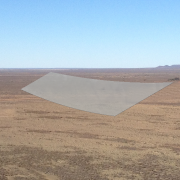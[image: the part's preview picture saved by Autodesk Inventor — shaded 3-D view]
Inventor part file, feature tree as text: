
AUTODESK INVENTOR PART (.ipt)
format: ipt  version: 2014 SP1 (Build 180222100, 222)  size: 152,576 bytes
history: native  units: in
note: dims shown in document units (in); Inventor stores cm internally (conversion verified against a paired STEP export)
features: sketch x3, sweep x1, extrude x1, other x1
ambient origin geometry x8: Origin, YZ Plane, XZ Plane, XY Plane, X Axis, Y Axis, Z Axis, Center Point
bodies: Body1 (feature_tree)
feature tree (6):
  sweep  "Sweep2"
  extrude  "Extrusion2"  TaperAngle=0.0deg  [1 undecoded]
  sketch  "Sketch3"  dims[d6=0.0in d7=277.0in d8=60.0in]
  other  "2D Equation Curve2"
  sketch  "Sketch4"  dims[d10=0.25in d11=0.0in]
  sketch  "Sketch7"  dims[d24=78.1in d25=167.1in d26=220.0in d27=1.1853in d28=2.0in d29=2.0in d30=200.0in d31=0.0in]
note: 1 required parameter value undecoded (feature->parameter linkage not recoverable at this tier; creation-order binding heuristic only, values carry confidence <= 0.55)
